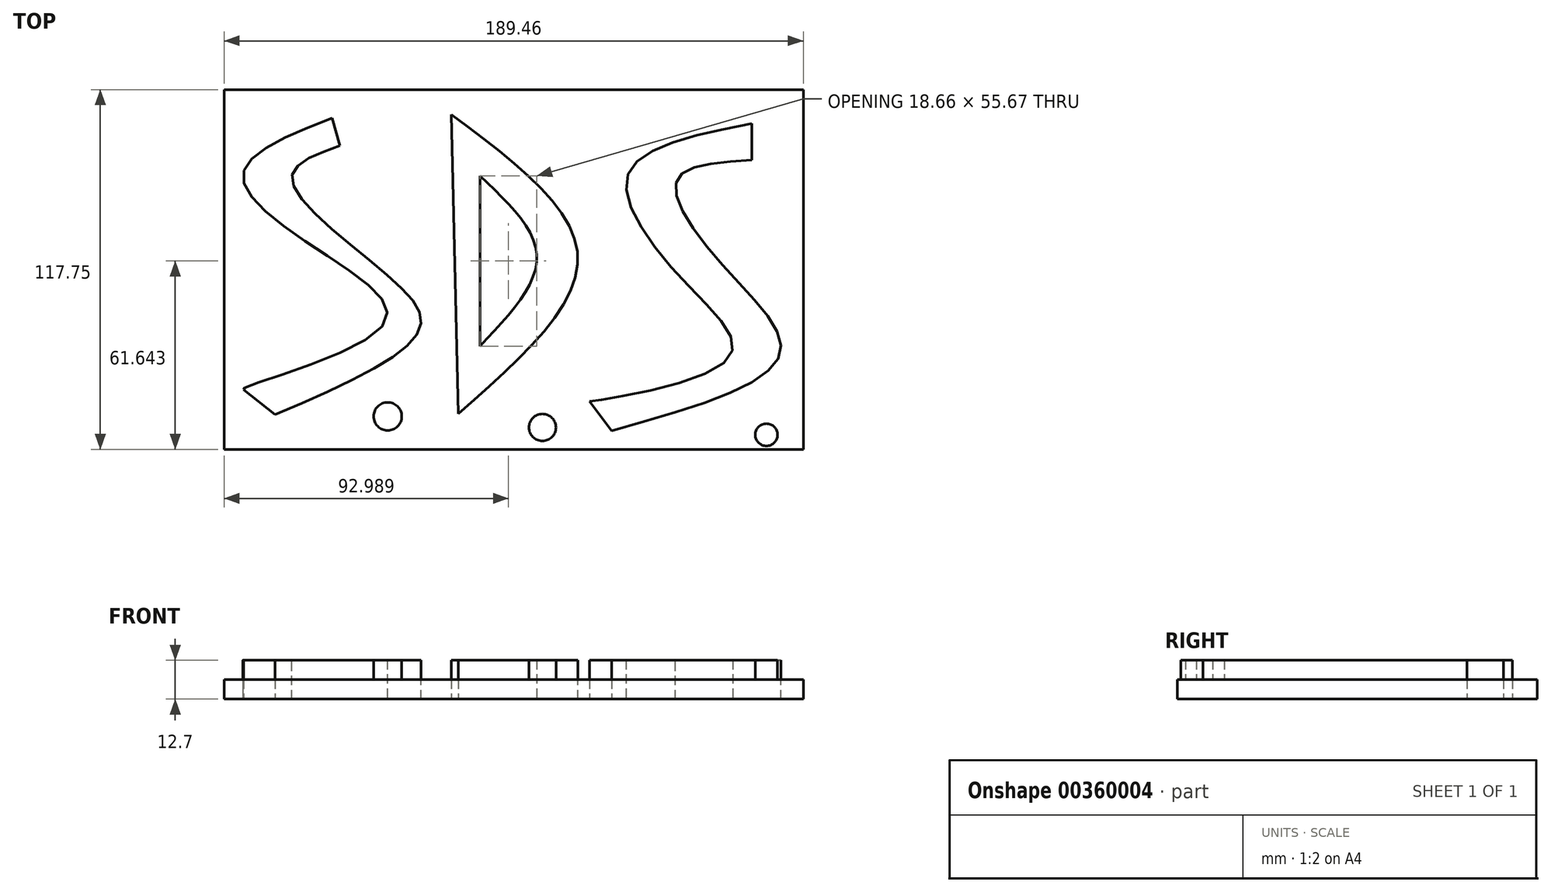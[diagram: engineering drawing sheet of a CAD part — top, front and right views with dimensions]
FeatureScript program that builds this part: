
annotation { "Feature Type Name" : "Feature", "Feature Type Description" : "" }
export const myFeature = defineFeature(function(context is Context, id is Id, definition is map)
    precondition{}
    {
        {
            var Q0;
            Q0=qCreatedBy(makeId("Top.planeOp"),FACE);
            var sketch = newSketch(context, id + "F0", { "sketchPlane" : qUnion([Q0])});
            skFitSpline(sketch, "E0", {"points": [v(-62.08, 45.32) * mm, v(-91.23, 26.67) * mm, v(-63.25, 0) * mm, v(-45.47, -22.59) * mm, v(-91.23, -43.28) * mm, v(-90.94, -43.58) * mm], "startDerivative": vector(-183.48, -72.42) * mm, "endDerivative": vector(23.06, -8.88) * mm});
            skLineSegment(sketch, "E1", {"start": v(-90.94, -43.58) * mm, "end": v(-80.74, -51.74) * mm});
            skLineSegment(sketch, "E2", {"start": v(-62.08, 45.32) * mm, "end": v(-59.46, 36.29) * mm});
            skFitSpline(sketch, "E3", {"points": [v(-59.46, 36.29) * mm, v(-75.2, 25.5) * mm, v(-43.72, -6.27) * mm, v(-33.52, -24.05) * mm, v(-80.74, -51.74) * mm], "startDerivative": vector(-125.71, -44.09) * mm, "endDerivative": vector(-202.74, -87.14) * mm});
            skSolve(sketch);
        }
        {
            var Q0;
            Q0=qCreatedBy(makeId("Top.planeOp"),FACE);
            var sketch = newSketch(context, id + "F1", { "sketchPlane" : qUnion([Q0])});
            skLineSegment(sketch, "E4", {"start": v(-23.03, 46.5) * mm, "end": v(-20.7, -51.45) * mm});
            skFitSpline(sketch, "E5", {"points": [v(-23.03, 46.5) * mm, v(18.36, 0) * mm, v(-20.7, -51.45) * mm], "startDerivative": vector(123.42, -91.84) * mm, "endDerivative": vector(-118, -104) * mm});
            skLineSegment(sketch, "E6", {"start": v(-13.7, 26.38) * mm, "end": v(-13.7, -29.3) * mm});
            skFitSpline(sketch, "E7", {"points": [v(-13.7, 26.38) * mm, v(4.96, 0) * mm, v(-13.7, -29.3) * mm], "startDerivative": vector(56.32, -52.79) * mm, "endDerivative": vector(-55.64, -58.52) * mm});
            skSolve(sketch);
        }
        {
            var Q0;
            Q0=qCreatedBy(makeId("Top.planeOp"),FACE);
            var sketch = newSketch(context, id + "F2", { "sketchPlane" : qUnion([Q0])});
            skFitSpline(sketch, "E8", {"points": [v(75.2, 43.58) * mm, v(34.69, 26.67) * mm, v(53.92, -8.9) * mm, v(67.33, -33.67) * mm, v(22.15, -47.36) * mm, v(21.57, -47.36) * mm], "startDerivative": vector(-218.61, -43.51) * mm, "endDerivative": vector(-7.33, 1.97) * mm});
            skLineSegment(sketch, "E9", {"start": v(75.2, 43.58) * mm, "end": v(75.2, 31.63) * mm});
            skLineSegment(sketch, "E10", {"start": v(22.15, -47.36) * mm, "end": v(29.44, -56.98) * mm});
            skFitSpline(sketch, "E11", {"points": [v(75.2, 31.63) * mm, v(50.72, 24.92) * mm, v(66.75, -3.93) * mm, v(84.53, -31.92) * mm, v(29.44, -56.98) * mm], "startDerivative": vector(-160.97, -10.1) * mm, "endDerivative": vector(-244.13, -68.5) * mm});
            skCircle(sketch, "E12", {"center": v(-42.56, -46.78) * mm, "radius": 4.44 * mm});
            skCircle(sketch, "E13", {"center": v(7.29, -48.82) * mm, "radius": 4.12 * mm});
            skSolve(sketch);
        }
        {
            var Q0;
            Q0=makeQuery(id+"F0.imprint","IMPRINT",FACE,{"disambiguationData":[TD([[makeQuery(id+"F0.imprint","IMPRINT",EDGE,{"derivedFrom":sQuery(id+"F0.wireOp",EDGE,"E0")}),1.0]])]});
            extrude(context, id + "F3", {"entities" : qUnion([Q0]), "depth" : 12.7 * mm});
        }
        {
            var Q0;
            Q0=makeQuery(id+"F1.imprint","IMPRINT",FACE,{"disambiguationData":[TD([[makeQuery(id+"F1.imprint","IMPRINT",EDGE,{"derivedFrom":sQuery(id+"F1.wireOp",EDGE,"E4")}),1.0]])]});
            extrude(context, id + "F4", {"entities" : qUnion([Q0]), "depth" : 12.7 * mm});
        }
        {
            var Q0;
            {var subQ0=sQuery(id+"F2.wireOp",EDGE,"E9");Q0=makeQuery(id+"F2.imprint","IMPRINT",FACE,{"disambiguationData":[TD([[makeQuery(id+"F2.imprint","IMPRINT",EDGE,{"derivedFrom":subQ0}),-1.0]])]});}
            extrude(context, id + "F5", {"entities" : qUnion([Q0]), "depth" : 12.7 * mm});
        }
        {
            var Q0;
            Q0=qCreatedBy(makeId("Top.planeOp"),FACE);
            var sketch = newSketch(context, id + "F6", { "sketchPlane" : qUnion([Q0])});
            skLineSegment(sketch, "E14.bottom", {"start": v(-97.36, 54.65) * mm, "end": v(92.1, 54.65) * mm});
            skLineSegment(sketch, "E14.top", {"start": v(-97.36, -63.1) * mm, "end": v(92.1, -63.1) * mm});
            skLineSegment(sketch, "E14.left", {"start": v(-97.36, 54.65) * mm, "end": v(-97.36, -63.1) * mm});
            skLineSegment(sketch, "E14.right", {"start": v(92.1, 54.65) * mm, "end": v(92.1, -63.1) * mm});
            skSolve(sketch);
        }
        {
            var Q0;
            Q0=makeQuery(id+"F6.imprint","IMPRINT",FACE,{"disambiguationData":[TD([[makeQuery(id+"F6.imprint","IMPRINT",EDGE,{"derivedFrom":sQuery(id+"F6.wireOp",EDGE,"E14.bottom")}),-1.0]])]});
            extrude(context, id + "F7", {"entities" : qUnion([Q0]), "depth" : 6.35 * mm});
        }
        {
            var Q0;
            Q0=makeQuery(id+"F7.opExtrude","CAP_FACE",FACE,{"disambiguationData":[OSD([sQuery(id+"F6.wireOp",EDGE,"E14.bottom"),sQuery(id+"F6.wireOp",EDGE,"E14.top"),sQuery(id+"F6.wireOp",EDGE,"E14.left"),sQuery(id+"F6.wireOp",EDGE,"E14.right")])],"isStart":false});
            var sketch = newSketch(context, id + "F8", { "sketchPlane" : qUnion([Q0])});
            skCircle(sketch, "E15", {"center": v(-43.84, -52.3) * mm, "radius": 4.6 * mm});
            skCircle(sketch, "E16", {"center": v(6.77, -55.91) * mm, "radius": 4.42 * mm});
            skCircle(sketch, "E17", {"center": v(80.03, -58.32) * mm, "radius": 3.65 * mm});
            skSolve(sketch);
        }
        {
            var Q0;
            Q0 = qSketchRegion(id + "F8", true);
            extrude(context, id + "F9", {"entities" : qUnion([Q0]), "operationType" : NewBodyOperationType.ADD, "depth" : 6.35 * mm});
        }
    });
